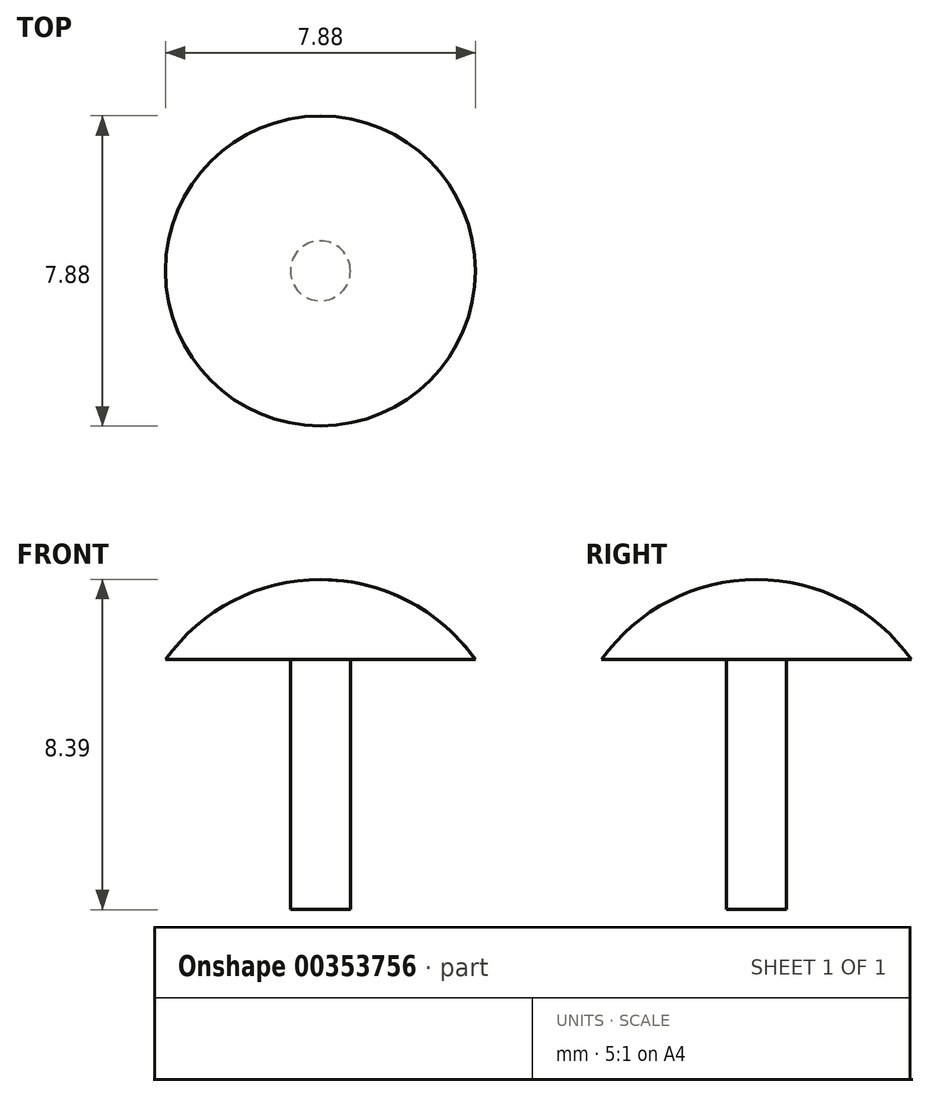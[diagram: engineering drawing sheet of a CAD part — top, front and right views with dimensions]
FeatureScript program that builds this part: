
annotation { "Feature Type Name" : "Feature", "Feature Type Description" : "" }
export const myFeature = defineFeature(function(context is Context, id is Id, definition is map)
    precondition{}
    {
        {
            var Q0;
            Q0=qCreatedBy(makeId("Front.planeOp"),FACE);
            var sketch = newSketch(context, id + "F0", { "sketchPlane" : qUnion([Q0])});
            skLineSegment(sketch, "E0.bottom", {"start": v(-0.76, -3.18) * mm, "end": v(0.76, -3.18) * mm});
            skLineSegment(sketch, "E0.top", {"start": v(-0.76, 3.17) * mm, "end": v(0.76, 3.17) * mm});
            skLineSegment(sketch, "E0.left", {"start": v(-0.76, -3.18) * mm, "end": v(-0.76, 3.17) * mm});
            skLineSegment(sketch, "E0.right", {"start": v(0.76, -3.18) * mm, "end": v(0.76, 3.17) * mm});
            skPoint(sketch, "E0.middle", {"position": v(0, 0) * mm});
            skLineSegment(sketch, "E1", {"start": v(-0.76, 3.17) * mm, "end": v(-3.94, 3.17) * mm});
            skLineSegment(sketch, "E2.MirrorCS", {"start": v(0.76, 3.17) * mm, "end": v(3.94, 3.17) * mm});
            skLineSegment(sketch, "E3", {"start": v(0, 3.17) * mm, "end": v(0, -3.17) * mm});
            skArc(sketch, "E4", {"start": v(3.94, 3.17) * mm, "mid": v(0, 5.2) * mm, "end": v(-3.94, 3.17) * mm});
            skLineSegment(sketch, "E5", {"start": v(0, 5.2) * mm, "end": v(0, -3.17) * mm});
            skSolve(sketch);
        }
        {
            var Q0;
            {var subQ0=sQuery(id+"F0.wireOp",EDGE,"E0.right");Q0=makeQuery(id+"F0.imprint","IMPRINT",FACE,{"disambiguationData":[TD([[makeQuery(id+"F0.imprint","IMPRINT",EDGE,{"derivedFrom":subQ0}),1.0]])]});}
            var Q1;
            {var subQ0=sQuery(id+"F0.wireOp",EDGE,"E2.MirrorCS");Q1=makeQuery(id+"F0.imprint","IMPRINT",FACE,{"disambiguationData":[TD([[makeQuery(id+"F0.imprint","IMPRINT",EDGE,{"derivedFrom":subQ0}),1.0]])]});}
            var Q2;
            Q2=sQuery(id+"F0.wireOp",EDGE,"E5");
            revolve(context, id + "F1", {"entities" : qUnion([Q0, Q1]), "axis" : qUnion([Q2]), "revolveType" : RevolveType.FULL});
        }
    });
